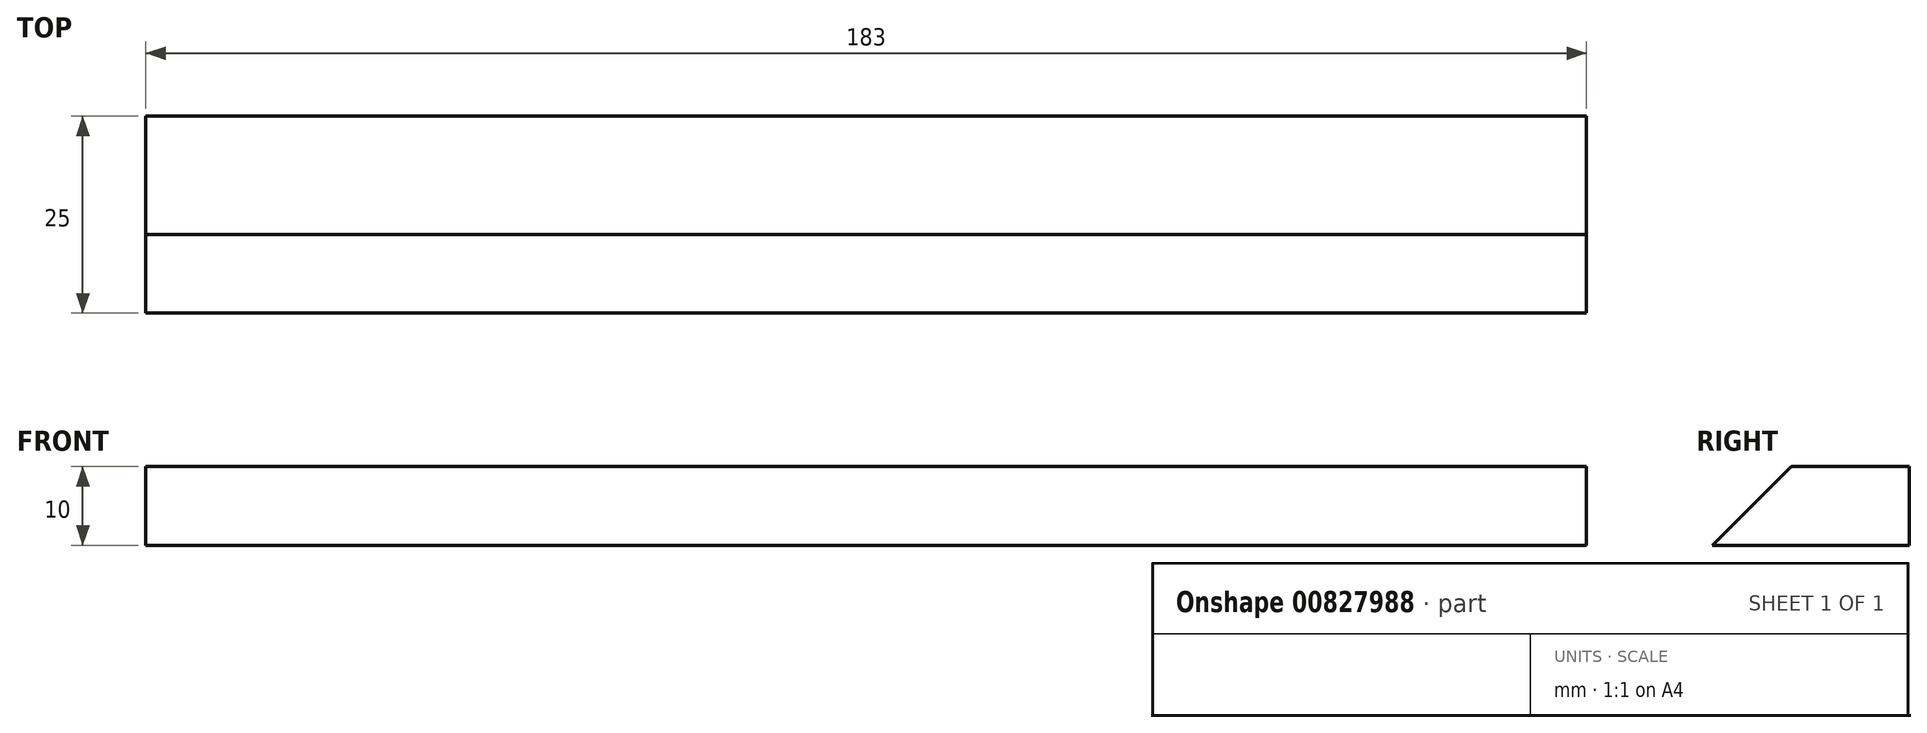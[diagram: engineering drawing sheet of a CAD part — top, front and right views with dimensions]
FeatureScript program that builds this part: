
annotation { "Feature Type Name" : "Feature", "Feature Type Description" : "" }
export const myFeature = defineFeature(function(context is Context, id is Id, definition is map)
    precondition{}
    {
        {
            var Q0;
            Q0=qCreatedBy(makeId("Right.planeOp"),FACE);
            var sketch = newSketch(context, id + "F0", { "sketchPlane" : qUnion([Q0])});
            skLineSegment(sketch, "E0.MirrorCS", {"start": v(-5, 5) * mm, "end": v(10, 5) * mm});
            skLineSegment(sketch, "E1.MirrorCS", {"start": v(-15, -5) * mm, "end": v(-5, 5) * mm});
            skLineSegment(sketch, "E2.MirrorCS", {"start": v(10, -5) * mm, "end": v(-15, -5) * mm});
            skLineSegment(sketch, "E3.MirrorCS", {"start": v(10, 5) * mm, "end": v(10, -5) * mm});
            skSolve(sketch);
        }
        {
            var Q0;
            Q0 = qSketchRegion(id + "F0", true);
            extrude(context, id + "F1", {"entities" : qUnion([Q0]), "endBound" : BoundingType.SYMMETRIC, "depth" : 183 * mm, "offsetDistance" : 25 * mm});
        }
    });
